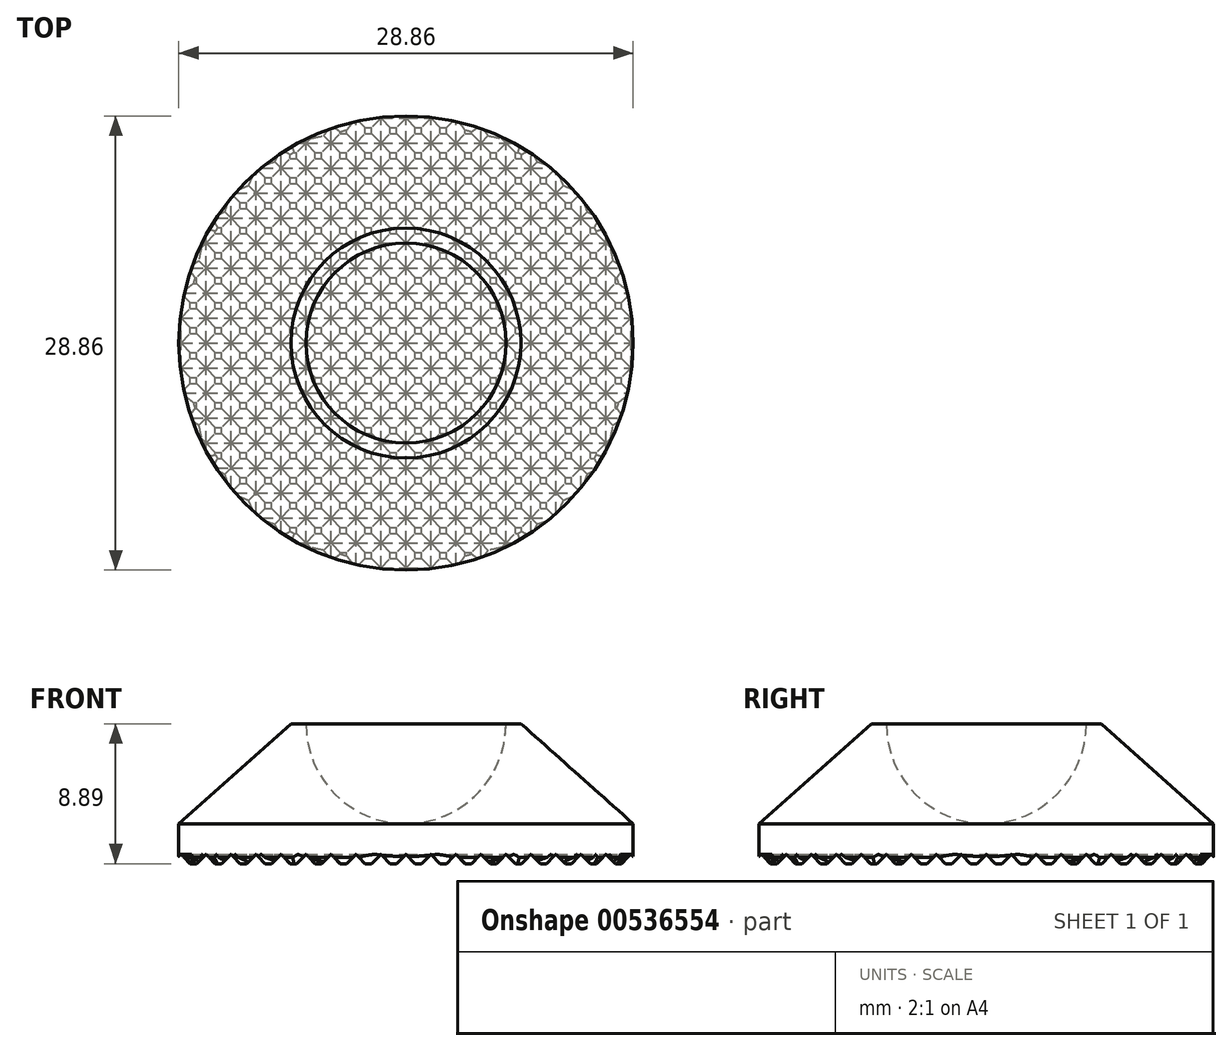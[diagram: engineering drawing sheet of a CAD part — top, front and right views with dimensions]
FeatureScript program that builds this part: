
annotation { "Feature Type Name" : "Feature", "Feature Type Description" : "" }
export const myFeature = defineFeature(function(context is Context, id is Id, definition is map)
    precondition{}
    {
        {
            var Q0;
            Q0=qCreatedBy(makeId("Front.planeOp"),FACE);
            var sketch = newSketch(context, id + "F0", { "sketchPlane" : qUnion([Q0])});
            skLineSegment(sketch, "E0", {"start": v(0, 0) * mm, "end": v(14.43, 0) * mm});
            skLineSegment(sketch, "E1", {"start": v(14.43, 0) * mm, "end": v(14.43, 2.54) * mm});
            skLineSegment(sketch, "E2", {"start": v(14.43, 2.54) * mm, "end": v(7.3, 8.9) * mm, "construction": true});
            skLineSegment(sketch, "E3", {"start": v(7.3, 8.9) * mm, "end": v(6.35, 8.9) * mm});
            skLineSegment(sketch, "E4", {"start": v(0, 0) * mm, "end": v(0, 2.54) * mm});
            skLineSegment(sketch, "E5", {"start": v(6.35, 8.9) * mm, "end": v(0, 8.9) * mm, "construction": true});
            skLineSegment(sketch, "E6", {"start": v(0, 8.9) * mm, "end": v(0, 2.54) * mm, "construction": true});
            skArc(sketch, "E7", {"start": v(0, 2.54) * mm, "mid": v(4.5, 4.4) * mm, "end": v(6.35, 8.89) * mm, "construction": true});
            skLineSegment(sketch, "E8", {"start": v(0, 8.9) * mm, "end": v(7.3, 8.9) * mm, "construction": true});
            skLineSegment(sketch, "E9", {"start": v(7.3, 8.9) * mm, "end": v(14.43, 2.54) * mm});
            skArc(sketch, "E10", {"start": v(0, 2.54) * mm, "mid": v(4.5, 4.4) * mm, "end": v(6.35, 8.9) * mm});
            skSolve(sketch);
        }
        {
            var Q0;
            Q0 = qSketchRegion(id + "F0", true);
            var Q1;
            Q1=sQuery(id+"F0.wireOp",EDGE,"E6");
            revolve(context, id + "F1", {"entities" : qUnion([Q0]), "axis" : qUnion([Q1]), "revolveType" : RevolveType.FULL});
        }
        {
            var Q0;
            Q0=makeQuery(id+"F1.opRevolve","SWEPT_EDGE",EDGE,{"disambiguationData":[OSD([sQuery(id+"F0.wireOp",EDGE,"E0"),sQuery(id+"F0.wireOp",EDGE,"E1")])]});
            chamfer(context, id + "F2", {"entities" : qUnion([Q0]), "width" : 0.4 * mm, "tangentPropagation" : true});
        }
        {
            var Q0;
            Q0=qCreatedBy(makeId("Front.planeOp"),FACE);
            var sketch = newSketch(context, id + "F3", { "sketchPlane" : qUnion([Q0])});
            skLineSegment(sketch, "E11", {"start": v(-15.28, 0) * mm, "end": v(-15.88, 0.6) * mm});
            skLineSegment(sketch, "E12", {"start": v(-15.88, 0.6) * mm, "end": v(-16.47, 0) * mm});
            skLineSegment(sketch, "E13", {"start": v(-16.47, 0) * mm, "end": v(-15.28, 0) * mm});
            skLineSegment(sketch, "E14.1.0.0", {"start": v(-13.7, 0) * mm, "end": v(-14.29, 0.6) * mm});
            skLineSegment(sketch, "E14.1.0.1", {"start": v(-14.29, 0.6) * mm, "end": v(-14.88, 0) * mm});
            skLineSegment(sketch, "E14.1.0.2", {"start": v(-14.88, 0) * mm, "end": v(-13.7, 0) * mm});
            skLineSegment(sketch, "E14.2.0.0", {"start": v(-12.1, 0) * mm, "end": v(-12.7, 0.6) * mm});
            skLineSegment(sketch, "E14.2.0.1", {"start": v(-12.7, 0.6) * mm, "end": v(-13.3, 0) * mm});
            skLineSegment(sketch, "E14.2.0.2", {"start": v(-13.3, 0) * mm, "end": v(-12.1, 0) * mm});
            skLineSegment(sketch, "E14.3.0.0", {"start": v(-10.52, 0) * mm, "end": v(-11.11, 0.6) * mm});
            skLineSegment(sketch, "E14.3.0.1", {"start": v(-11.11, 0.6) * mm, "end": v(-11.7, 0) * mm});
            skLineSegment(sketch, "E14.3.0.2", {"start": v(-11.7, 0) * mm, "end": v(-10.52, 0) * mm});
            skLineSegment(sketch, "E14.4.0.0", {"start": v(-8.93, 0) * mm, "end": v(-9.53, 0.6) * mm});
            skLineSegment(sketch, "E14.4.0.1", {"start": v(-9.53, 0.6) * mm, "end": v(-10.12, 0) * mm});
            skLineSegment(sketch, "E14.4.0.2", {"start": v(-10.12, 0) * mm, "end": v(-8.93, 0) * mm});
            skLineSegment(sketch, "E14.5.0.0", {"start": v(-7.34, 0) * mm, "end": v(-7.94, 0.6) * mm});
            skLineSegment(sketch, "E14.5.0.1", {"start": v(-7.94, 0.6) * mm, "end": v(-8.53, 0) * mm});
            skLineSegment(sketch, "E14.5.0.2", {"start": v(-8.53, 0) * mm, "end": v(-7.34, 0) * mm});
            skLineSegment(sketch, "E14.6.0.0", {"start": v(-5.75, 0) * mm, "end": v(-6.35, 0.6) * mm});
            skLineSegment(sketch, "E14.6.0.1", {"start": v(-6.35, 0.6) * mm, "end": v(-6.95, 0) * mm});
            skLineSegment(sketch, "E14.6.0.2", {"start": v(-6.95, 0) * mm, "end": v(-5.75, 0) * mm});
            skLineSegment(sketch, "E14.7.0.0", {"start": v(-4.17, 0) * mm, "end": v(-4.76, 0.6) * mm});
            skLineSegment(sketch, "E14.7.0.1", {"start": v(-4.76, 0.6) * mm, "end": v(-5.36, 0) * mm});
            skLineSegment(sketch, "E14.7.0.2", {"start": v(-5.36, 0) * mm, "end": v(-4.17, 0) * mm});
            skLineSegment(sketch, "E14.8.0.0", {"start": v(-2.58, 0) * mm, "end": v(-3.18, 0.6) * mm});
            skLineSegment(sketch, "E14.8.0.1", {"start": v(-3.18, 0.6) * mm, "end": v(-3.77, 0) * mm});
            skLineSegment(sketch, "E14.8.0.2", {"start": v(-3.77, 0) * mm, "end": v(-2.58, 0) * mm});
            skLineSegment(sketch, "E14.9.0.0", {"start": v(-1, 0) * mm, "end": v(-1.59, 0.6) * mm});
            skLineSegment(sketch, "E14.9.0.1", {"start": v(-1.59, 0.6) * mm, "end": v(-2.18, 0) * mm});
            skLineSegment(sketch, "E14.9.0.2", {"start": v(-2.18, 0) * mm, "end": v(-1, 0) * mm});
            skLineSegment(sketch, "E14.10.0.0", {"start": v(0.6, 0) * mm, "end": v(0, 0.6) * mm});
            skLineSegment(sketch, "E14.10.0.1", {"start": v(0, 0.6) * mm, "end": v(-0.6, 0) * mm});
            skLineSegment(sketch, "E14.10.0.2", {"start": v(-0.6, 0) * mm, "end": v(0.6, 0) * mm});
            skLineSegment(sketch, "E14.11.0.0", {"start": v(2.18, 0) * mm, "end": v(1.59, 0.6) * mm});
            skLineSegment(sketch, "E14.11.0.1", {"start": v(1.59, 0.6) * mm, "end": v(1, 0) * mm});
            skLineSegment(sketch, "E14.11.0.2", {"start": v(1, 0) * mm, "end": v(2.18, 0) * mm});
            skLineSegment(sketch, "E14.12.0.0", {"start": v(3.77, 0) * mm, "end": v(3.17, 0.6) * mm});
            skLineSegment(sketch, "E14.12.0.1", {"start": v(3.17, 0.6) * mm, "end": v(2.58, 0) * mm});
            skLineSegment(sketch, "E14.12.0.2", {"start": v(2.58, 0) * mm, "end": v(3.77, 0) * mm});
            skLineSegment(sketch, "E14.13.0.0", {"start": v(5.36, 0) * mm, "end": v(4.76, 0.6) * mm});
            skLineSegment(sketch, "E14.13.0.1", {"start": v(4.76, 0.6) * mm, "end": v(4.17, 0) * mm});
            skLineSegment(sketch, "E14.13.0.2", {"start": v(4.17, 0) * mm, "end": v(5.36, 0) * mm});
            skLineSegment(sketch, "E14.14.0.0", {"start": v(6.95, 0) * mm, "end": v(6.35, 0.6) * mm});
            skLineSegment(sketch, "E14.14.0.1", {"start": v(6.35, 0.6) * mm, "end": v(5.75, 0) * mm});
            skLineSegment(sketch, "E14.14.0.2", {"start": v(5.75, 0) * mm, "end": v(6.95, 0) * mm});
            skLineSegment(sketch, "E14.15.0.0", {"start": v(8.53, 0) * mm, "end": v(7.94, 0.6) * mm});
            skLineSegment(sketch, "E14.15.0.1", {"start": v(7.94, 0.6) * mm, "end": v(7.34, 0) * mm});
            skLineSegment(sketch, "E14.15.0.2", {"start": v(7.34, 0) * mm, "end": v(8.53, 0) * mm});
            skLineSegment(sketch, "E14.16.0.0", {"start": v(10.12, 0) * mm, "end": v(9.52, 0.6) * mm});
            skLineSegment(sketch, "E14.16.0.1", {"start": v(9.52, 0.6) * mm, "end": v(8.93, 0) * mm});
            skLineSegment(sketch, "E14.16.0.2", {"start": v(8.93, 0) * mm, "end": v(10.12, 0) * mm});
            skLineSegment(sketch, "E14.17.0.0", {"start": v(11.7, 0) * mm, "end": v(11.11, 0.6) * mm});
            skLineSegment(sketch, "E14.17.0.1", {"start": v(11.11, 0.6) * mm, "end": v(10.52, 0) * mm});
            skLineSegment(sketch, "E14.17.0.2", {"start": v(10.52, 0) * mm, "end": v(11.7, 0) * mm});
            skLineSegment(sketch, "E14.18.0.0", {"start": v(13.3, 0) * mm, "end": v(12.7, 0.6) * mm});
            skLineSegment(sketch, "E14.18.0.1", {"start": v(12.7, 0.6) * mm, "end": v(12.1, 0) * mm});
            skLineSegment(sketch, "E14.18.0.2", {"start": v(12.1, 0) * mm, "end": v(13.3, 0) * mm});
            skLineSegment(sketch, "E14.19.0.0", {"start": v(14.88, 0) * mm, "end": v(14.29, 0.6) * mm});
            skLineSegment(sketch, "E14.19.0.1", {"start": v(14.29, 0.6) * mm, "end": v(13.7, 0) * mm});
            skLineSegment(sketch, "E14.19.0.2", {"start": v(13.7, 0) * mm, "end": v(14.88, 0) * mm});
            skLineSegment(sketch, "E14.direction1", {"start": v(-16.47, 0) * mm, "end": v(-14.88, 0) * mm, "construction": true});
            skSolve(sketch);
        }
        {
            var Q0;
            Q0 = qSketchRegion(id + "F3", true);
            extrude(context, id + "F4", {"entities" : qUnion([Q0]), "operationType" : NewBodyOperationType.REMOVE, "endBound" : BoundingType.SYMMETRIC, "depth" : 50.8 * mm, "offsetDistance" : 25.4 * mm});
        }
        {
            var Q0;
            Q0=qCreatedBy(makeId("Right.planeOp"),FACE);
            var sketch = newSketch(context, id + "F5", { "sketchPlane" : qUnion([Q0])});
            skLineSegment(sketch, "E15", {"start": v(-15.28, 0) * mm, "end": v(-15.88, 0.6) * mm});
            skLineSegment(sketch, "E16", {"start": v(-15.88, 0.6) * mm, "end": v(-16.47, 0) * mm});
            skLineSegment(sketch, "E17", {"start": v(-16.47, 0) * mm, "end": v(-15.28, 0) * mm});
            skLineSegment(sketch, "E18.1.0.0", {"start": v(-13.7, 0) * mm, "end": v(-14.29, 0.6) * mm});
            skLineSegment(sketch, "E18.1.0.1", {"start": v(-14.29, 0.6) * mm, "end": v(-14.88, 0) * mm});
            skLineSegment(sketch, "E18.1.0.2", {"start": v(-14.88, 0) * mm, "end": v(-13.7, 0) * mm});
            skLineSegment(sketch, "E18.2.0.0", {"start": v(-12.1, 0) * mm, "end": v(-12.7, 0.6) * mm});
            skLineSegment(sketch, "E18.2.0.1", {"start": v(-12.7, 0.6) * mm, "end": v(-13.3, 0) * mm});
            skLineSegment(sketch, "E18.2.0.2", {"start": v(-13.3, 0) * mm, "end": v(-12.1, 0) * mm});
            skLineSegment(sketch, "E18.3.0.0", {"start": v(-10.52, 0) * mm, "end": v(-11.11, 0.6) * mm});
            skLineSegment(sketch, "E18.3.0.1", {"start": v(-11.11, 0.6) * mm, "end": v(-11.7, 0) * mm});
            skLineSegment(sketch, "E18.3.0.2", {"start": v(-11.7, 0) * mm, "end": v(-10.52, 0) * mm});
            skLineSegment(sketch, "E18.4.0.0", {"start": v(-8.93, 0) * mm, "end": v(-9.52, 0.6) * mm});
            skLineSegment(sketch, "E18.4.0.1", {"start": v(-9.52, 0.6) * mm, "end": v(-10.12, 0) * mm});
            skLineSegment(sketch, "E18.4.0.2", {"start": v(-10.12, 0) * mm, "end": v(-8.93, 0) * mm});
            skLineSegment(sketch, "E18.5.0.0", {"start": v(-7.34, 0) * mm, "end": v(-7.94, 0.6) * mm});
            skLineSegment(sketch, "E18.5.0.1", {"start": v(-7.94, 0.6) * mm, "end": v(-8.53, 0) * mm});
            skLineSegment(sketch, "E18.5.0.2", {"start": v(-8.53, 0) * mm, "end": v(-7.34, 0) * mm});
            skLineSegment(sketch, "E18.6.0.0", {"start": v(-5.75, 0) * mm, "end": v(-6.35, 0.6) * mm});
            skLineSegment(sketch, "E18.6.0.1", {"start": v(-6.35, 0.6) * mm, "end": v(-6.95, 0) * mm});
            skLineSegment(sketch, "E18.6.0.2", {"start": v(-6.95, 0) * mm, "end": v(-5.75, 0) * mm});
            skLineSegment(sketch, "E18.7.0.0", {"start": v(-4.17, 0) * mm, "end": v(-4.76, 0.6) * mm});
            skLineSegment(sketch, "E18.7.0.1", {"start": v(-4.76, 0.6) * mm, "end": v(-5.36, 0) * mm});
            skLineSegment(sketch, "E18.7.0.2", {"start": v(-5.36, 0) * mm, "end": v(-4.17, 0) * mm});
            skLineSegment(sketch, "E18.8.0.0", {"start": v(-2.58, 0) * mm, "end": v(-3.17, 0.6) * mm});
            skLineSegment(sketch, "E18.8.0.1", {"start": v(-3.17, 0.6) * mm, "end": v(-3.77, 0) * mm});
            skLineSegment(sketch, "E18.8.0.2", {"start": v(-3.77, 0) * mm, "end": v(-2.58, 0) * mm});
            skLineSegment(sketch, "E18.9.0.0", {"start": v(-1, 0) * mm, "end": v(-1.59, 0.6) * mm});
            skLineSegment(sketch, "E18.9.0.1", {"start": v(-1.59, 0.6) * mm, "end": v(-2.18, 0) * mm});
            skLineSegment(sketch, "E18.9.0.2", {"start": v(-2.18, 0) * mm, "end": v(-1, 0) * mm});
            skLineSegment(sketch, "E18.10.0.0", {"start": v(0.6, 0) * mm, "end": v(0, 0.6) * mm});
            skLineSegment(sketch, "E18.10.0.1", {"start": v(0, 0.6) * mm, "end": v(-0.6, 0) * mm});
            skLineSegment(sketch, "E18.10.0.2", {"start": v(-0.6, 0) * mm, "end": v(0.6, 0) * mm});
            skLineSegment(sketch, "E18.11.0.0", {"start": v(2.18, 0) * mm, "end": v(1.59, 0.6) * mm});
            skLineSegment(sketch, "E18.11.0.1", {"start": v(1.59, 0.6) * mm, "end": v(1, 0) * mm});
            skLineSegment(sketch, "E18.11.0.2", {"start": v(1, 0) * mm, "end": v(2.18, 0) * mm});
            skLineSegment(sketch, "E18.12.0.0", {"start": v(3.77, 0) * mm, "end": v(3.18, 0.6) * mm});
            skLineSegment(sketch, "E18.12.0.1", {"start": v(3.18, 0.6) * mm, "end": v(2.58, 0) * mm});
            skLineSegment(sketch, "E18.12.0.2", {"start": v(2.58, 0) * mm, "end": v(3.77, 0) * mm});
            skLineSegment(sketch, "E18.13.0.0", {"start": v(5.36, 0) * mm, "end": v(4.76, 0.6) * mm});
            skLineSegment(sketch, "E18.13.0.1", {"start": v(4.76, 0.6) * mm, "end": v(4.17, 0) * mm});
            skLineSegment(sketch, "E18.13.0.2", {"start": v(4.17, 0) * mm, "end": v(5.36, 0) * mm});
            skLineSegment(sketch, "E18.14.0.0", {"start": v(6.95, 0) * mm, "end": v(6.35, 0.6) * mm});
            skLineSegment(sketch, "E18.14.0.1", {"start": v(6.35, 0.6) * mm, "end": v(5.75, 0) * mm});
            skLineSegment(sketch, "E18.14.0.2", {"start": v(5.75, 0) * mm, "end": v(6.95, 0) * mm});
            skLineSegment(sketch, "E18.15.0.0", {"start": v(8.53, 0) * mm, "end": v(7.94, 0.6) * mm});
            skLineSegment(sketch, "E18.15.0.1", {"start": v(7.94, 0.6) * mm, "end": v(7.34, 0) * mm});
            skLineSegment(sketch, "E18.15.0.2", {"start": v(7.34, 0) * mm, "end": v(8.53, 0) * mm});
            skLineSegment(sketch, "E18.16.0.0", {"start": v(10.12, 0) * mm, "end": v(9.53, 0.6) * mm});
            skLineSegment(sketch, "E18.16.0.1", {"start": v(9.53, 0.6) * mm, "end": v(8.93, 0) * mm});
            skLineSegment(sketch, "E18.16.0.2", {"start": v(8.93, 0) * mm, "end": v(10.12, 0) * mm});
            skLineSegment(sketch, "E18.17.0.0", {"start": v(11.7, 0) * mm, "end": v(11.11, 0.6) * mm});
            skLineSegment(sketch, "E18.17.0.1", {"start": v(11.11, 0.6) * mm, "end": v(10.52, 0) * mm});
            skLineSegment(sketch, "E18.17.0.2", {"start": v(10.52, 0) * mm, "end": v(11.7, 0) * mm});
            skLineSegment(sketch, "E18.18.0.0", {"start": v(13.3, 0) * mm, "end": v(12.7, 0.6) * mm});
            skLineSegment(sketch, "E18.18.0.1", {"start": v(12.7, 0.6) * mm, "end": v(12.1, 0) * mm});
            skLineSegment(sketch, "E18.18.0.2", {"start": v(12.1, 0) * mm, "end": v(13.3, 0) * mm});
            skLineSegment(sketch, "E18.19.0.0", {"start": v(14.88, 0) * mm, "end": v(14.29, 0.6) * mm});
            skLineSegment(sketch, "E18.19.0.1", {"start": v(14.29, 0.6) * mm, "end": v(13.7, 0) * mm});
            skLineSegment(sketch, "E18.19.0.2", {"start": v(13.7, 0) * mm, "end": v(14.88, 0) * mm});
            skLineSegment(sketch, "E18.direction1", {"start": v(-16.47, 0) * mm, "end": v(-14.88, 0) * mm, "construction": true});
            skSolve(sketch);
        }
        {
            var Q0;
            Q0 = qSketchRegion(id + "F5", true);
            extrude(context, id + "F6", {"entities" : qUnion([Q0]), "operationType" : NewBodyOperationType.REMOVE, "endBound" : BoundingType.SYMMETRIC, "oppositeDirection" : true, "depth" : 50.8 * mm, "offsetDistance" : 25.4 * mm});
        }
    });
